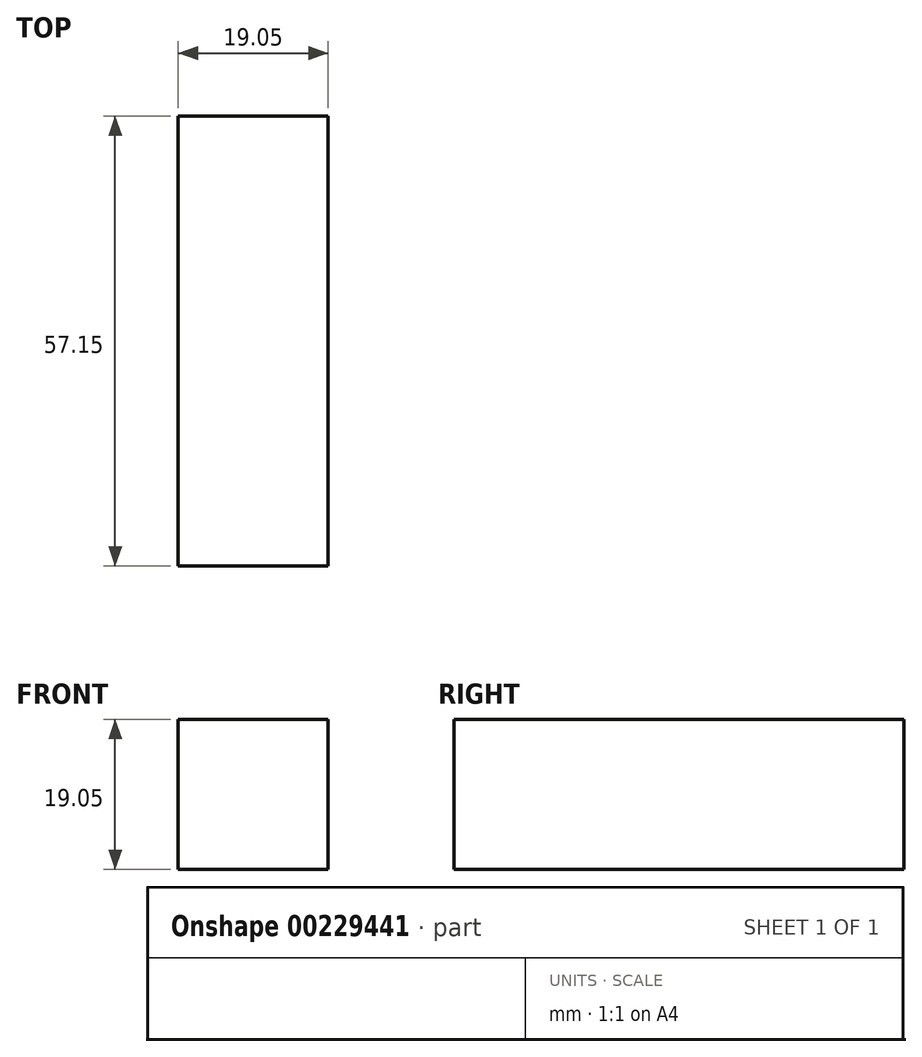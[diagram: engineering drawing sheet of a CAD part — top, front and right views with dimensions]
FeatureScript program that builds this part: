
annotation { "Feature Type Name" : "Feature", "Feature Type Description" : "" }
export const myFeature = defineFeature(function(context is Context, id is Id, definition is map)
    precondition{}
    {
        {
            var Q0;
            Q0=qCreatedBy(makeId("Top.planeOp"),FACE);
            var sketch = newSketch(context, id + "F0", { "sketchPlane" : qUnion([Q0])});
            skLineSegment(sketch, "E0.bottom", {"start": v(-60.14, 57.15) * mm, "end": v(-41.1, 57.15) * mm});
            skLineSegment(sketch, "E0.top", {"start": v(-60.14, 0) * mm, "end": v(-41.1, 0) * mm});
            skLineSegment(sketch, "E0.left", {"start": v(-60.14, 57.15) * mm, "end": v(-60.14, 0) * mm});
            skLineSegment(sketch, "E0.right", {"start": v(-41.1, 57.15) * mm, "end": v(-41.1, 0) * mm});
            skSolve(sketch);
        }
        {
            var Q0;
            Q0 = qSketchRegion(id + "F0", true);
            extrude(context, id + "F1", {"entities" : qUnion([Q0]), "depth" : 19.05 * mm});
        }
    });
